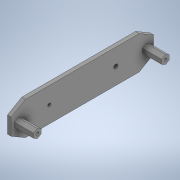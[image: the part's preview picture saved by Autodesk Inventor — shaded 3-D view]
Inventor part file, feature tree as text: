
AUTODESK INVENTOR PART (.ipt)
format: ipt  version: 2020 (Build 240168000, 168)  size: 227,328 bytes
history: native  units: in
note: dims shown in document units (in); Inventor stores cm internally (conversion verified against a paired STEP export)
features: extrude x7, sketch x7, plane x1
ambient origin geometry x8: Origin, YZ Plane, XZ Plane, XY Plane, X Axis, Y Axis, Z Axis, Center Point
bodies: Solid1 (feature_tree)
feature tree (15):
  extrude  "Extrusion1"  Depth=5.9055in
  extrude  "Extrusion3"  TaperAngle=0.0deg  [1 undecoded]
  extrude  "Extrusion4"  Depth=0.7874in
  plane  "Work Plane1"
  extrude  "Extrusion5"  Depth=0.122in
  extrude  "Extrusion6"  Depth=0.2402in
  extrude  "Extrusion7"  [1 undecoded]
  extrude  "Extrusion8"  Depth=0.0866in TaperAngle=0.0deg
  sketch  "Sketch1"  dims[d0=1.378in d1=5.9055in]
  sketch  "Sketch2"  dims[d2=0.1575in d3=0.0in]
  sketch  "Sketch3"  dims[d8=0.315in d9=0.7874in]
  sketch  "Sketch4"  dims[d10=0.0in d12=0.122in]
  sketch  "Sketch5"  dims[d13=0.0in d14=0.0in d15=0.2402in]
  sketch  "Sketch8"  dims[d16=0.0866in d17=-0.2233in]
  sketch  "Sketch9"  dims[d18=-0.3937in d19=0.0866in d20=0.0in d26=1.5748in d27=0.1654in d28=0.122in d29=1.5748in d30=0.0in d31=0.0in d32=0.2402in d33=0.0866in d34=-0.2233in]
note: 2 required parameter values undecoded (feature->parameter linkage not recoverable at this tier; creation-order binding heuristic only, values carry confidence <= 0.55)
